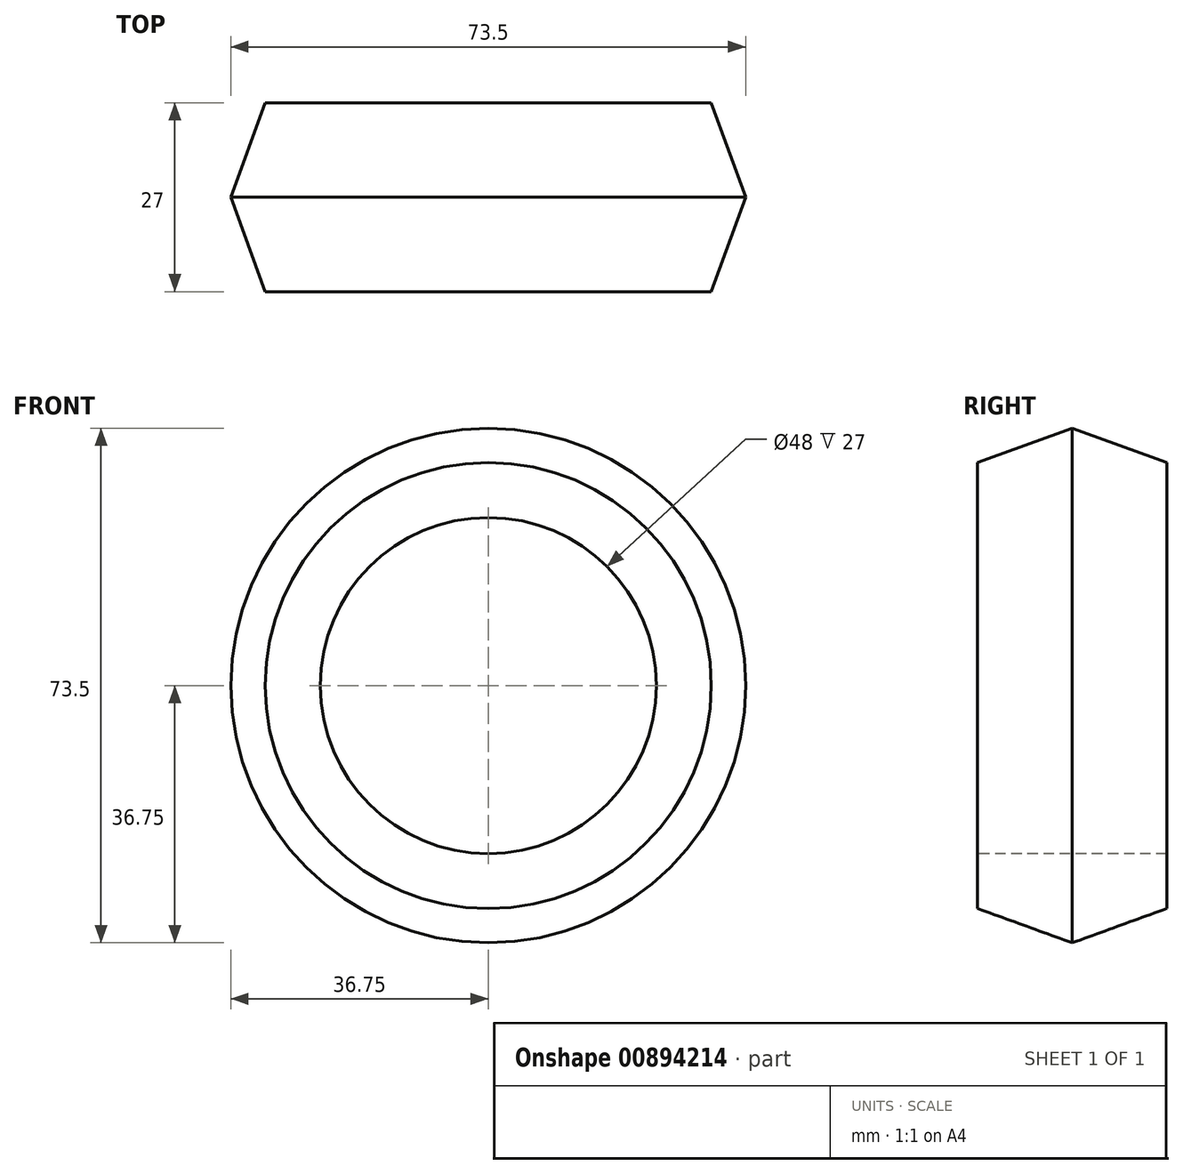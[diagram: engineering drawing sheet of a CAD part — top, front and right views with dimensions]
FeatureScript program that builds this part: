
annotation { "Feature Type Name" : "Feature", "Feature Type Description" : "" }
export const myFeature = defineFeature(function(context is Context, id is Id, definition is map)
    precondition{}
    {
        {
            var Q0;
            Q0=qCreatedBy(makeId("Right.planeOp"),FACE);
            var sketch = newSketch(context, id + "F0", { "sketchPlane" : qUnion([Q0])});
            skLineSegment(sketch, "E0", {"start": v(0, 0) * mm, "end": v(0, 24) * mm, "construction": true});
            skLineSegment(sketch, "E1", {"start": v(0, 24) * mm, "end": v(0, 31.85) * mm});
            skLineSegment(sketch, "E2", {"start": v(0, 31.85) * mm, "end": v(13.5, 36.75) * mm});
            skLineSegment(sketch, "E3", {"start": v(13.5, 36.75) * mm, "end": v(27, 31.85) * mm});
            skLineSegment(sketch, "E4", {"start": v(27, 31.85) * mm, "end": v(27, 24) * mm});
            skLineSegment(sketch, "E5", {"start": v(27, 24) * mm, "end": v(0, 24) * mm});
            skLineSegment(sketch, "E6", {"start": v(13.5, 36.75) * mm, "end": v(13.5, 24) * mm, "construction": true});
            skLineSegment(sketch, "E7", {"start": v(0, 0) * mm, "end": v(27, 0) * mm});
            skSolve(sketch);
        }
        {
            var Q0;
            Q0=makeQuery(id+"F0.imprint","IMPRINT",FACE,{"disambiguationData":[TD([[makeQuery(id+"F0.imprint","IMPRINT",EDGE,{"derivedFrom":sQuery(id+"F0.wireOp",EDGE,"E1")}),-1.0]])]});
            var Q1;
            Q1=sQuery(id+"F0.wireOp",EDGE,"E7");
            revolve(context, id + "F1", {"surfaceOperationType" : NewSurfaceOperationType.NEW, "entities" : qUnion([Q0]), "axis" : qUnion([Q1]), "revolveType" : RevolveType.FULL});
        }
    });
